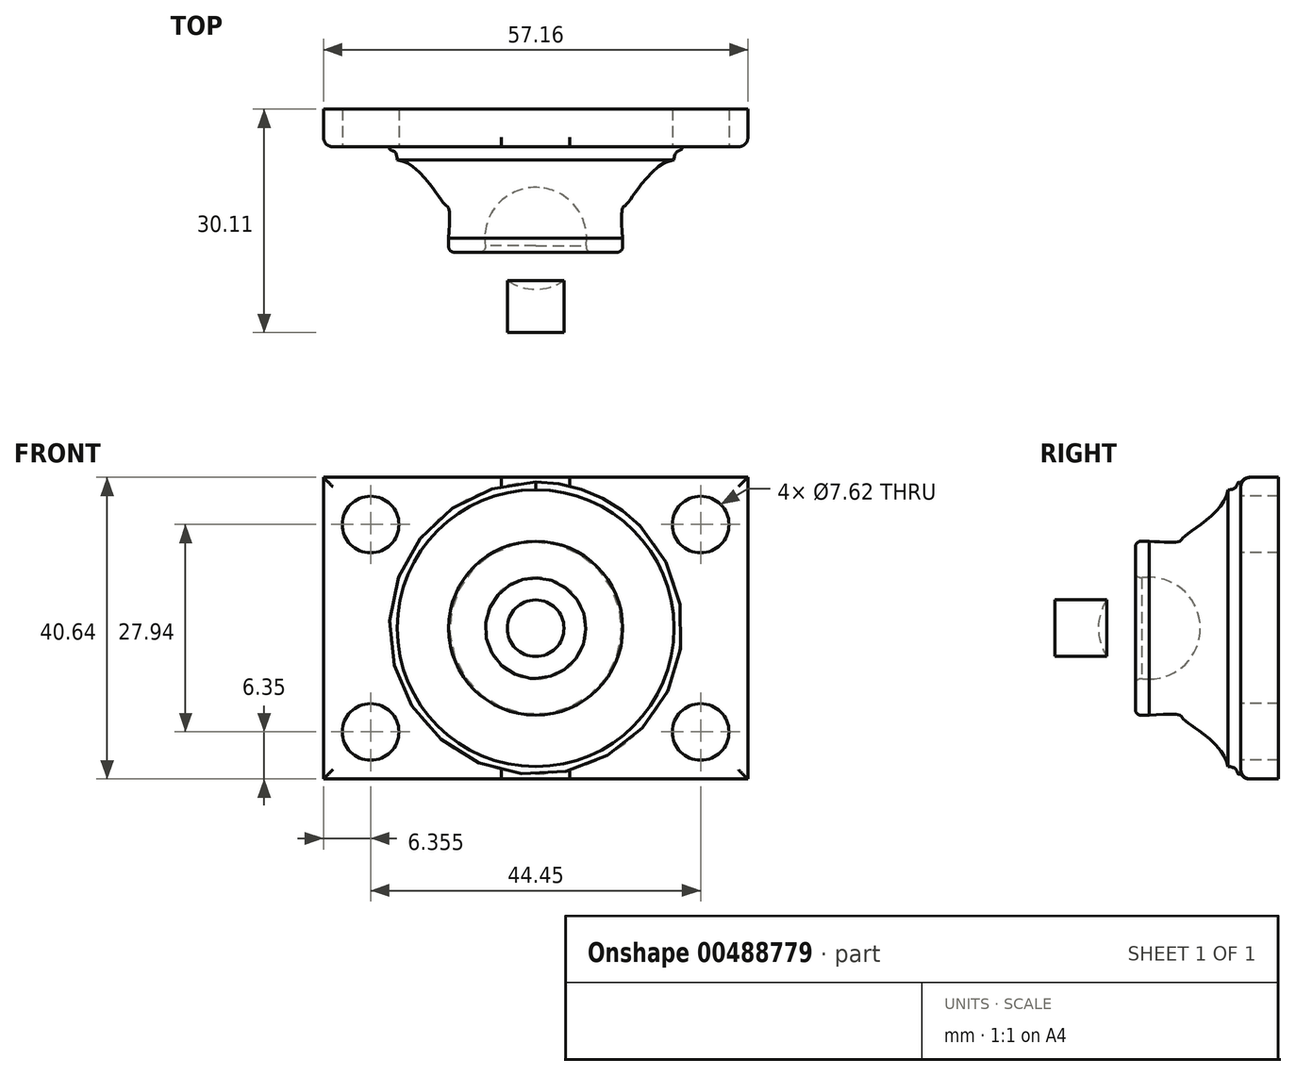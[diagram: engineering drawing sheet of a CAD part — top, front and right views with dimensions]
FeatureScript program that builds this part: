
annotation { "Feature Type Name" : "Feature", "Feature Type Description" : "" }
export const myFeature = defineFeature(function(context is Context, id is Id, definition is map)
    precondition{}
    {
        {
            var Q0;
            Q0=qCreatedBy(makeId("Front.planeOp"),FACE);
            var sketch = newSketch(context, id + "F0", { "sketchPlane" : qUnion([Q0])});
            skArc(sketch, "E0", {"start": v(0, -6.35) * mm, "mid": v(6.35, 0) * mm, "end": v(0, 6.35) * mm});
            skLineSegment(sketch, "E1", {"start": v(0, 6.35) * mm, "end": v(0, -6.35) * mm});
            skSolve(sketch);
        }
        {
            var Q0;
            Q0=makeQuery(id+"F0.imprint","IMPRINT",FACE,{"disambiguationData":[TD([[makeQuery(id+"F0.imprint","IMPRINT",EDGE,{"derivedFrom":sQuery(id+"F0.wireOp",EDGE,"E0")}),1.0]])]});
            var Q1;
            Q1=sQuery(id+"F0.wireOp",EDGE,"E1");
            revolve(context, id + "F1", {"entities" : qUnion([Q0]), "axis" : qUnion([Q1]), "revolveType" : RevolveType.FULL});
        }
        {
            var Q0;
            Q0=qCreatedBy(makeId("Front.planeOp"),FACE);
            var sketch = newSketch(context, id + "F2", { "sketchPlane" : qUnion([Q0])});
            skCircle(sketch, "E2", {"center": v(0, 0) * mm, "radius": 3.81 * mm});
            skSolve(sketch);
        }
        {
            var Q0;
            Q0 = qSketchRegion(id + "F2", true);
            extrude(context, id + "F3", {"entities" : qUnion([Q0]), "operationType" : NewBodyOperationType.ADD, "depth" : 12.7 * mm});
        }
        {
            var Q0;
            Q0=qCreatedBy(makeId("Right.planeOp"),FACE);
            var sketch = newSketch(context, id + "F4", { "sketchPlane" : qUnion([Q0])});
            skLineSegment(sketch, "E3", {"start": v(-1.87, 11.72) * mm, "end": v(-1.87, 0) * mm});
            skLineSegment(sketch, "E4", {"start": v(-1.87, 0) * mm, "end": v(12.33, 0) * mm});
            skLineSegment(sketch, "E5", {"start": v(-1.87, 11.72) * mm, "end": v(0, 11.72) * mm});
            skFitSpline(sketch, "E6", {"points": [v(0, 11.72) * mm, v(4.13, 11.72) * mm, v(4.58, 12.23) * mm, v(10.59, 18.64) * mm], "startDerivative": vector(16.04, -1.2) * mm, "endDerivative": vector(2.64, 18.2) * mm});
            skFitSpline(sketch, "E7", {"points": [v(10.59, 18.64) * mm, v(12.33, 19.6) * mm], "startDerivative": vector(5.22, 0) * mm, "endDerivative": vector(2.31, -1.3) * mm});
            skLineSegment(sketch, "E8", {"start": v(12.33, 19.6) * mm, "end": v(12.33, 0) * mm});
            skLineSegment(sketch, "E9", {"start": v(12.33, 0) * mm, "end": v(-1.87, 0) * mm});
            skSolve(sketch);
        }
        {
            var Q0;
            Q0=makeQuery(id+"F4.imprint","IMPRINT",FACE,{"disambiguationData":[TD([[makeQuery(id+"F4.imprint","IMPRINT",EDGE,{"derivedFrom":sQuery(id+"F4.wireOp",EDGE,"E3")}),1.0]])]});
            var Q1;
            Q1=sQuery(id+"F4.wireOp",EDGE,"E9");
            revolve(context, id + "F5", {"entities" : qUnion([Q0]), "axis" : qUnion([Q1]), "revolveType" : RevolveType.FULL});
        }
        {
            var Q0;
            Q0=makeQuery(id+"F5.opRevolve","SWEPT_FACE",FACE,{"disambiguationData":[OSD([sQuery(id+"F4.wireOp",EDGE,"E8")])]});
            var sketch = newSketch(context, id + "F6", { "sketchPlane" : qUnion([Q0])});
            skLineSegment(sketch, "E10.bottom", {"start": v(28.58, 20.32) * mm, "end": v(-28.57, 20.32) * mm});
            skLineSegment(sketch, "E10.top", {"start": v(28.58, -20.32) * mm, "end": v(-28.58, -20.32) * mm});
            skLineSegment(sketch, "E10.left", {"start": v(28.58, 20.32) * mm, "end": v(28.58, -20.32) * mm});
            skLineSegment(sketch, "E10.right", {"start": v(-28.57, 20.32) * mm, "end": v(-28.58, -20.32) * mm});
            skPoint(sketch, "E10.middle", {"position": v(0, 0) * mm});
            skLineSegment(sketch, "E11", {"start": v(0, 0) * mm, "end": v(0, 20.32) * mm, "construction": true});
            skLineSegment(sketch, "E12", {"start": v(0, 20.32) * mm, "end": v(0, -20.32) * mm, "construction": true});
            skLineSegment(sketch, "E13", {"start": v(0, 0) * mm, "end": v(28.58, 0) * mm, "construction": true});
            skLineSegment(sketch, "E14", {"start": v(28.58, 0) * mm, "end": v(-28.58, 0) * mm, "construction": true});
            skCircle(sketch, "E15", {"center": v(22.23, 13.97) * mm, "radius": 3.81 * mm});
            skLineSegment(sketch, "E16.MirrorCS", {"start": v(0, -20.32) * mm, "end": v(0, 20.32) * mm, "construction": true});
            skCircle(sketch, "E17.MirrorC", {"center": v(22.23, -13.97) * mm, "radius": 3.81 * mm});
            skCircle(sketch, "E18.MirrorC", {"center": v(-22.23, 13.97) * mm, "radius": 3.81 * mm});
            skCircle(sketch, "E19.MirrorC", {"center": v(-22.23, -13.97) * mm, "radius": 3.81 * mm});
            skSolve(sketch);
        }
        {
            var Q0;
            Q0 = qSketchRegion(id + "F6", true);
            extrude(context, id + "F7", {"entities" : qUnion([Q0]), "operationType" : NewBodyOperationType.ADD, "depth" : 5.08 * mm});
        }
        {
            var Q0;
            Q0 = qSketchRegion(id + "F0", true);
            var sketch = newSketch(context, id + "F8", { "sketchPlane" : qUnion([Q0])});
            skLineSegment(sketch, "E20", {"start": v(0, -6.35) * mm, "end": v(0, 6.35) * mm});
            skArc(sketch, "E21.0", {"start": v(0, -6.86) * mm, "mid": v(6.86, 0) * mm, "end": v(0, 6.86) * mm});
            skLineSegment(sketch, "E22", {"start": v(0, 6.86) * mm, "end": v(0, 6.35) * mm});
            skLineSegment(sketch, "E23", {"start": v(0, -6.86) * mm, "end": v(0, -6.35) * mm});
            skPoint(sketch, "E24.MirrorCS.end.orphan", {"position": v(0, 6.35) * mm});
            skPoint(sketch, "E24.MirrorCS.start.orphan", {"position": v(0, -6.35) * mm});
            skSolve(sketch);
        }
        {
            var Q0;
            Q0 = qSketchRegion(id + "F8", true);
            var Q1;
            Q1=sQuery(id+"F8.wireOp",EDGE,"E20");
            revolve(context, id + "F9", {"operationType" : NewBodyOperationType.REMOVE, "entities" : qUnion([Q0]), "axis" : qUnion([Q1]), "revolveType" : RevolveType.FULL, "oppositeDirection" : true});
        }
        {
            var Q0;
            Q0=makeQuery(id+"F7.opExtrude","CAP_EDGE",EDGE,{"disambiguationData":[OSD([sQuery(id+"F6.wireOp",EDGE,"E10.bottom")])],"isStart":true});
            var Q1;
            Q1=makeQuery(id+"F7.opExtrude","CAP_EDGE",EDGE,{"disambiguationData":[OSD([sQuery(id+"F6.wireOp",EDGE,"E10.left")])],"isStart":true});
            var Q2;
            Q2=makeQuery(id+"F7.opExtrude","CAP_EDGE",EDGE,{"disambiguationData":[OSD([sQuery(id+"F6.wireOp",EDGE,"E10.top")])],"isStart":true});
            var Q3;
            Q3=makeQuery(id+"F7.opExtrude","CAP_EDGE",EDGE,{"disambiguationData":[OSD([sQuery(id+"F6.wireOp",EDGE,"E10.right")])],"isStart":true});
            fillet(context, id + "F10", {"entities" : qUnion([Q0, Q1, Q2, Q3]), "radius" : 1.27 * mm, "tangentPropagation" : true, "allowEdgeOverflow" : false});
        }
        {
            var Q0;
            Q0=makeQuery(id+"F9.boolean.opBoolean","INTERSECT",EDGE,{"derivedFrom":[makeQuery(id+"F5.opRevolve","SWEPT_FACE",FACE,{"disambiguationData":[OSD([sQuery(id+"F4.wireOp",EDGE,"E3")])]}),makeQuery(id+"F9.opRevolve","SWEPT_FACE",FACE,{"disambiguationData":[OSD([sQuery(id+"F8.wireOp",EDGE,"E21.0")])]})]});
            var Q1;
            Q1=makeQuery(id+"F5.opRevolve","SWEPT_EDGE",EDGE,{"disambiguationData":[OSD([sQuery(id+"F4.wireOp",EDGE,"E3"),sQuery(id+"F4.wireOp",EDGE,"E5")])]});
            fillet(context, id + "F11", {"entities" : qUnion([Q0, Q1]), "radius" : 0.76 * mm, "tangentPropagation" : true, "allowEdgeOverflow" : false});
        }
    });
